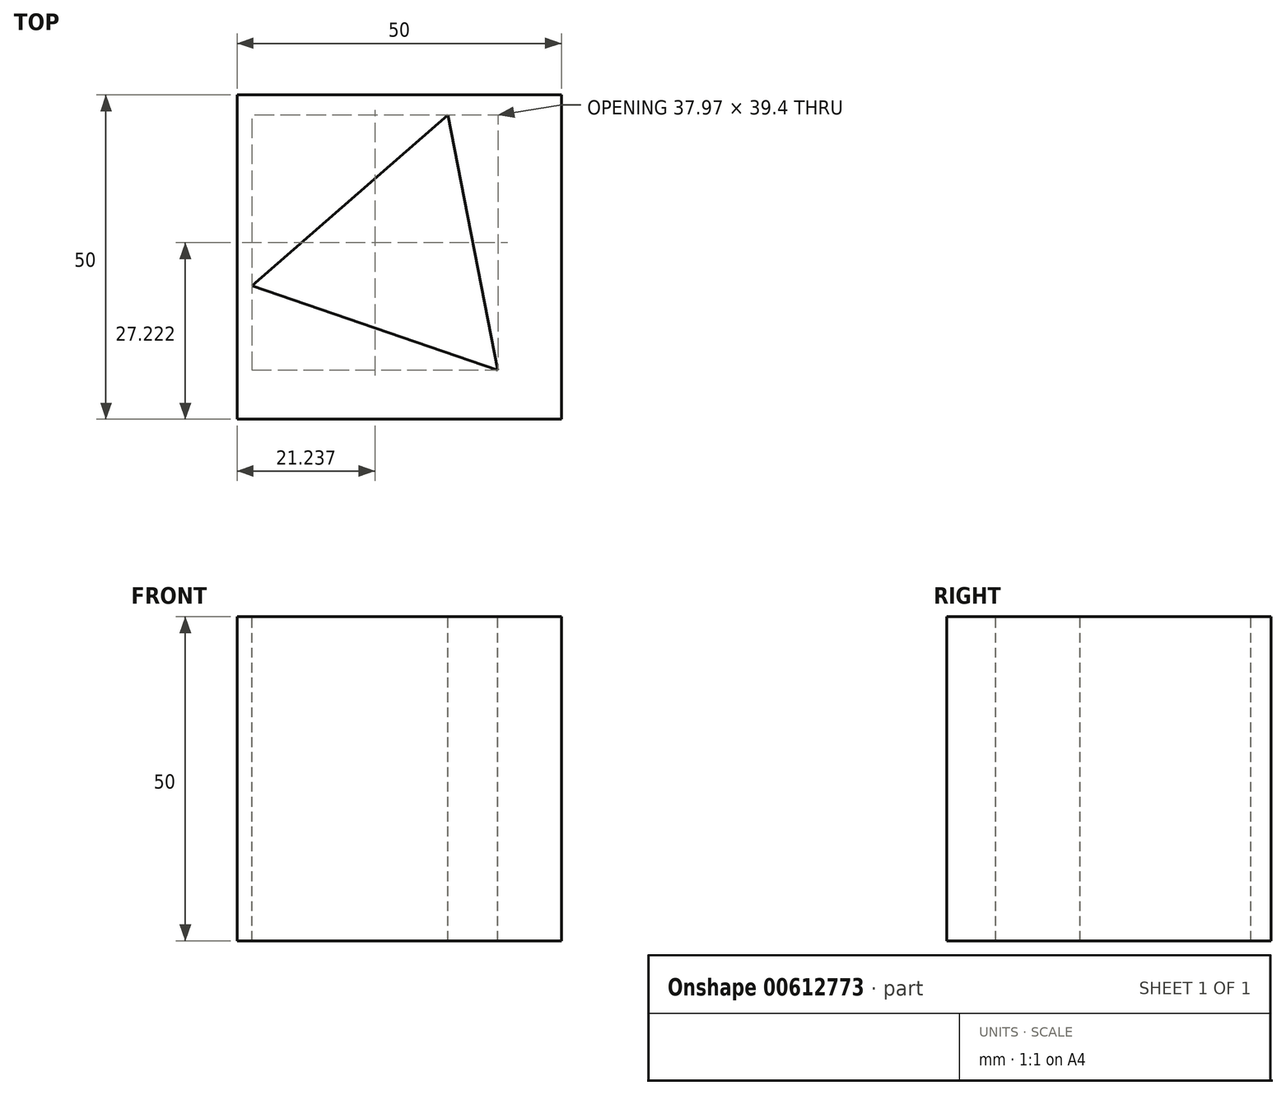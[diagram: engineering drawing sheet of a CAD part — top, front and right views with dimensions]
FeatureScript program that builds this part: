
annotation { "Feature Type Name" : "Feature", "Feature Type Description" : "" }
export const myFeature = defineFeature(function(context is Context, id is Id, definition is map)
    precondition{}
    {
        {
            var Q0;
            Q0=qCreatedBy(makeId("Top.planeOp"),FACE);
            var sketch = newSketch(context, id + "F0", { "sketchPlane" : qUnion([Q0])});
            skLineSegment(sketch, "E0.bottom", {"start": v(-25, 25) * mm, "end": v(25, 25) * mm});
            skLineSegment(sketch, "E0.top", {"start": v(-25, -25) * mm, "end": v(25, -25) * mm});
            skLineSegment(sketch, "E0.left", {"start": v(-25, 25) * mm, "end": v(-25, -25) * mm});
            skLineSegment(sketch, "E0.right", {"start": v(25, 25) * mm, "end": v(25, -25) * mm});
            skPoint(sketch, "E0.middle", {"position": v(0, 0) * mm});
            skSolve(sketch);
        }
        {
            var Q0;
            Q0 = qSketchRegion(id + "F0", true);
            extrude(context, id + "F1", {"entities" : qUnion([Q0]), "depth" : 50 * mm, "offsetDistance" : 25 * mm});
        }
        {
            var Q0;
            Q0=makeQuery(id+"F1.opExtrude","CAP_FACE",FACE,{"disambiguationData":[OSD([sQuery(id+"F0.wireOp",EDGE,"E0.bottom"),sQuery(id+"F0.wireOp",EDGE,"E0.top"),sQuery(id+"F0.wireOp",EDGE,"E0.left"),sQuery(id+"F0.wireOp",EDGE,"E0.right")])],"isStart":false});
            var sketch = newSketch(context, id + "F2", { "sketchPlane" : qUnion([Q0])});
            skLineSegment(sketch, "E1", {"start": v(0, 25) * mm, "end": v(0, 0) * mm});
            skCircle(sketch, "E2.cCircle", {"center": v(0, 0) * mm, "radius": 11.59 * mm, "construction": true});
            skLineSegment(sketch, "E2.0", {"start": v(-22.75, -4.44) * mm, "end": v(7.53, 21.92) * mm});
            skLineSegment(sketch, "E2.1", {"start": v(7.53, 21.92) * mm, "end": v(15.22, -17.48) * mm});
            skLineSegment(sketch, "E2.2", {"start": v(15.22, -17.48) * mm, "end": v(-22.75, -4.44) * mm});
            skPoint(sketch, "E2.0.midPoint", {"position": v(-7.61, 8.74) * mm});
            skSolve(sketch);
        }
        {
            var Q0;
            {var subQ3=sQuery(id+"F2.wireOp",EDGE,"E2.1");Q0=makeQuery(id+"F2.imprint","IMPRINT",FACE,{"disambiguationData":[TD([[makeQuery(id+"F2.imprint","IMPRINT",EDGE,{"derivedFrom":subQ3}),-1.0]])]});}
            extrude(context, id + "F3", {"entities" : qUnion([Q0]), "operationType" : NewBodyOperationType.REMOVE, "oppositeDirection" : true, "depth" : 55 * mm, "offsetDistance" : 25 * mm});
        }
    });
